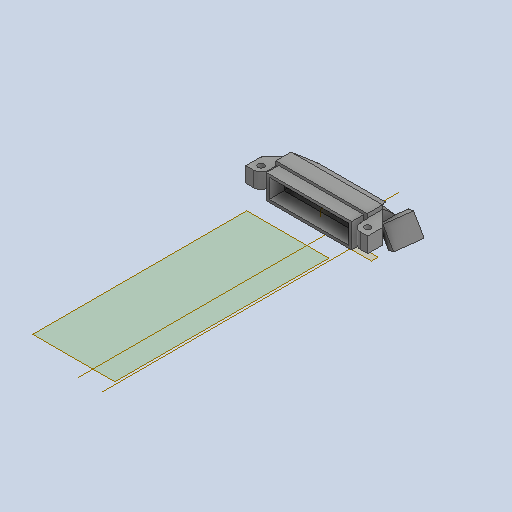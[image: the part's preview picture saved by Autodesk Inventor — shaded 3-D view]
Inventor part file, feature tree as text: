
AUTODESK INVENTOR PART (.ipt)
format: ipt  version: 2022 (Build 260153000, 153)  size: 325,120 bytes
history: native  units: in
note: dims shown in document units (in); Inventor stores cm internally (conversion verified against a paired STEP export)
features: sketch x7, other x5, plane x3
ambient origin geometry x8: Origin, YZ Plane, XZ Plane, XY Plane, X Axis, Y Axis, Z Axis, Center Point
bodies: Solid1 (feature_tree)
feature tree (15):
  other  "4010 part cooling duct.ipt"
  other  "Solid1::4010 part cooling duct.ipt"
  other  "TaggingFeature1"
  sketch  "Sketch1"  dims[d0=0.3937in]
  sketch  "Sketch2"
  sketch  "Sketch3"
  sketch  "Sketch4"
  sketch  "Sketch5"
  sketch  "Sketch7"
  sketch  "Sketch8"
  plane  "Work Plane1"
  plane  "Work Plane2"
  plane  "Work Plane5"
  other  "Work Axis1"
  other  "Work Axis2"
